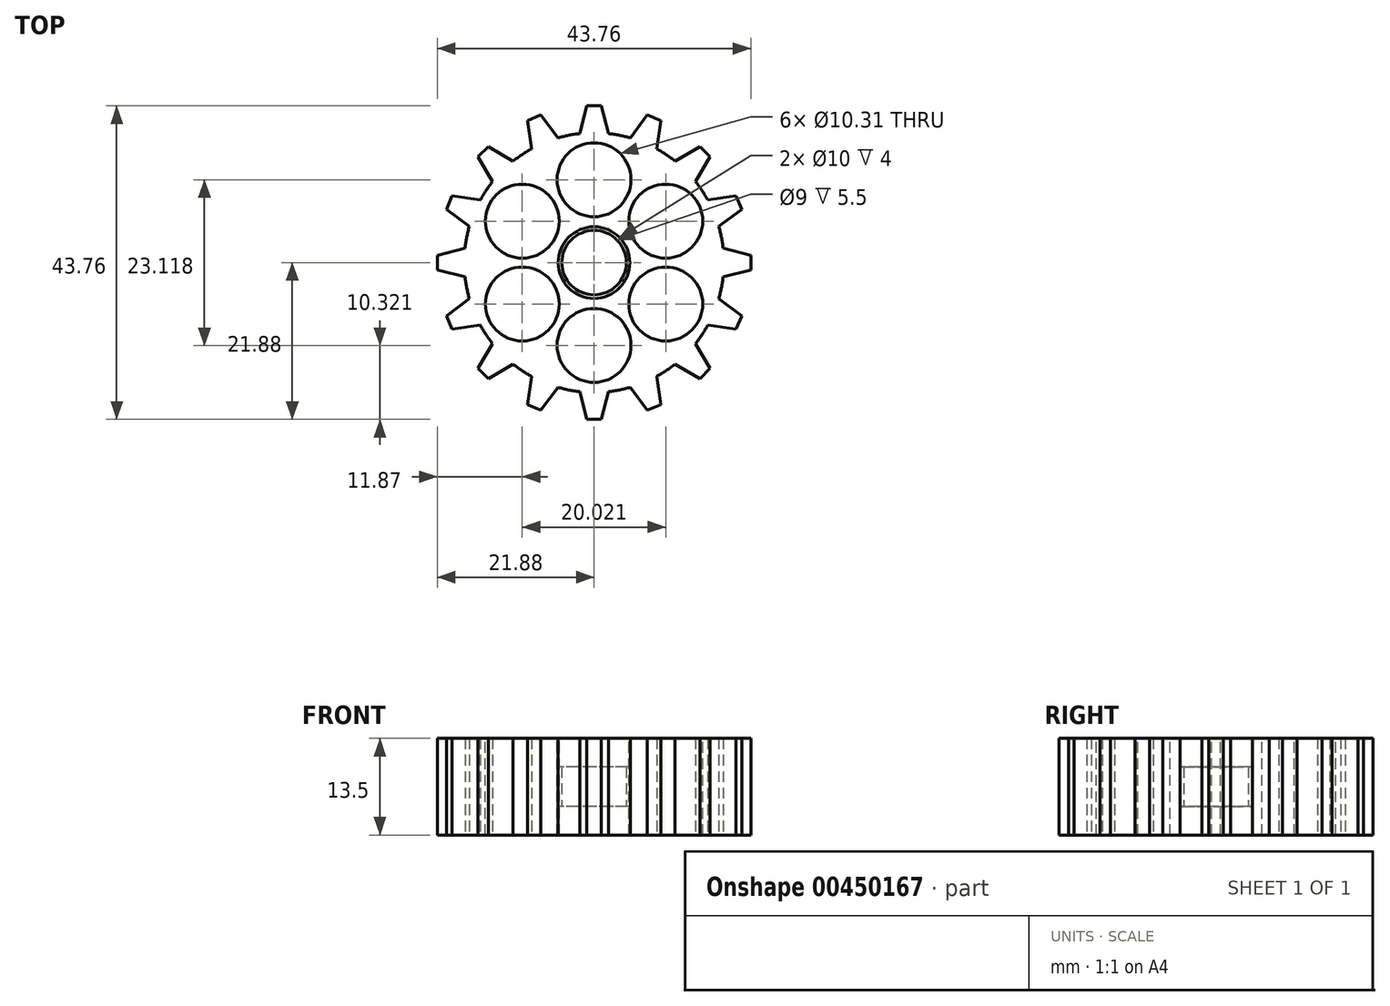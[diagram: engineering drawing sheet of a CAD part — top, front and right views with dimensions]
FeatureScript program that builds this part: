
annotation { "Feature Type Name" : "Feature", "Feature Type Description" : "" }
export const myFeature = defineFeature(function(context is Context, id is Id, definition is map)
    precondition{}
    {
        {
            var Q0;
            Q0=qCreatedBy(makeId("Top.planeOp"),FACE);
            var sketch = newSketch(context, id + "F0", { "sketchPlane" : qUnion([Q0])});
            skLineSegment(sketch, "E0", {"start": v(-18, -2) * mm, "end": v(-21.88, -1) * mm});
            skLineSegment(sketch, "E1", {"start": v(-21.88, -1) * mm, "end": v(-21.88, 1) * mm});
            skLineSegment(sketch, "E2", {"start": v(-21.88, 1) * mm, "end": v(-18, 2) * mm});
            skCircle(sketch, "E3", {"center": v(0, 0) * mm, "radius": 20 * mm, "construction": true});
            skPoint(sketch, "E4", {"position": v(-19.94, 1.5) * mm});
            skPoint(sketch, "E5", {"position": v(-19.94, -1.5) * mm});
            skArc(sketch, "E6", {"start": v(-17.4, 5.04) * mm, "mid": v(-17.77, 3.53) * mm, "end": v(-18, 2) * mm});
            skPoint(sketch, "E7", {"position": v(-21.88, 0) * mm});
            skLineSegment(sketch, "E8.1.0", {"start": v(-15.87, -8.74) * mm, "end": v(-19.83, -9.3) * mm});
            skLineSegment(sketch, "E8.1.1", {"start": v(-20.6, -7.45) * mm, "end": v(-17.4, -5.04) * mm});
            skArc(sketch, "E8.1.2", {"start": v(-18, -2) * mm, "mid": v(-17.77, -3.53) * mm, "end": v(-17.4, -5.04) * mm});
            skPoint(sketch, "E8.1.3", {"position": v(-19, -6.25) * mm});
            skPoint(sketch, "E8.1.4", {"position": v(-17.85, -9.02) * mm});
            skPoint(sketch, "E8.1.5", {"position": v(-20.21, -8.37) * mm});
            skLineSegment(sketch, "E8.1.6", {"start": v(-19.83, -9.3) * mm, "end": v(-20.6, -7.45) * mm});
            skLineSegment(sketch, "E8.2.0", {"start": v(-11.32, -14.15) * mm, "end": v(-14.76, -16.18) * mm});
            skLineSegment(sketch, "E8.2.1", {"start": v(-16.18, -14.76) * mm, "end": v(-14.15, -11.32) * mm});
            skArc(sketch, "E8.2.2", {"start": v(-15.87, -8.74) * mm, "mid": v(-15.06, -10.07) * mm, "end": v(-14.15, -11.32) * mm});
            skPoint(sketch, "E8.2.3", {"position": v(-15.16, -13.04) * mm});
            skPoint(sketch, "E8.2.4", {"position": v(-13.04, -15.16) * mm});
            skPoint(sketch, "E8.2.5", {"position": v(-15.47, -15.47) * mm});
            skLineSegment(sketch, "E8.2.6", {"start": v(-14.76, -16.18) * mm, "end": v(-16.18, -14.76) * mm});
            skLineSegment(sketch, "E8.3.0", {"start": v(-5.04, -17.4) * mm, "end": v(-7.45, -20.6) * mm});
            skLineSegment(sketch, "E8.3.1", {"start": v(-9.3, -19.83) * mm, "end": v(-8.74, -15.87) * mm});
            skArc(sketch, "E8.3.2", {"start": v(-11.32, -14.15) * mm, "mid": v(-10.07, -15.06) * mm, "end": v(-8.74, -15.87) * mm});
            skPoint(sketch, "E8.3.3", {"position": v(-9.02, -17.85) * mm});
            skPoint(sketch, "E8.3.4", {"position": v(-6.25, -19) * mm});
            skPoint(sketch, "E8.3.5", {"position": v(-8.37, -20.21) * mm});
            skLineSegment(sketch, "E8.3.6", {"start": v(-7.45, -20.6) * mm, "end": v(-9.3, -19.83) * mm});
            skLineSegment(sketch, "E8.4.0", {"start": v(2, -18) * mm, "end": v(1, -21.88) * mm});
            skLineSegment(sketch, "E8.4.1", {"start": v(-1, -21.88) * mm, "end": v(-2, -18) * mm});
            skArc(sketch, "E8.4.2", {"start": v(-5.04, -17.4) * mm, "mid": v(-3.53, -17.77) * mm, "end": v(-2, -18) * mm});
            skPoint(sketch, "E8.4.3", {"position": v(-1.5, -19.94) * mm});
            skPoint(sketch, "E8.4.4", {"position": v(1.5, -19.94) * mm});
            skPoint(sketch, "E8.4.5", {"position": v(0, -21.88) * mm});
            skLineSegment(sketch, "E8.4.6", {"start": v(1, -21.88) * mm, "end": v(-1, -21.88) * mm});
            skLineSegment(sketch, "E8.5.0", {"start": v(8.74, -15.87) * mm, "end": v(9.3, -19.83) * mm});
            skLineSegment(sketch, "E8.5.1", {"start": v(7.45, -20.6) * mm, "end": v(5.04, -17.4) * mm});
            skArc(sketch, "E8.5.2", {"start": v(2, -18) * mm, "mid": v(3.53, -17.77) * mm, "end": v(5.04, -17.4) * mm});
            skPoint(sketch, "E8.5.3", {"position": v(6.25, -19) * mm});
            skPoint(sketch, "E8.5.4", {"position": v(9.02, -17.85) * mm});
            skPoint(sketch, "E8.5.5", {"position": v(8.37, -20.21) * mm});
            skLineSegment(sketch, "E8.5.6", {"start": v(9.3, -19.83) * mm, "end": v(7.45, -20.6) * mm});
            skLineSegment(sketch, "E8.6.0", {"start": v(14.15, -11.32) * mm, "end": v(16.18, -14.76) * mm});
            skLineSegment(sketch, "E8.6.1", {"start": v(14.76, -16.18) * mm, "end": v(11.32, -14.15) * mm});
            skArc(sketch, "E8.6.2", {"start": v(8.74, -15.87) * mm, "mid": v(10.07, -15.06) * mm, "end": v(11.32, -14.15) * mm});
            skPoint(sketch, "E8.6.3", {"position": v(13.04, -15.16) * mm});
            skPoint(sketch, "E8.6.4", {"position": v(15.16, -13.04) * mm});
            skPoint(sketch, "E8.6.5", {"position": v(15.47, -15.47) * mm});
            skLineSegment(sketch, "E8.6.6", {"start": v(16.18, -14.76) * mm, "end": v(14.76, -16.18) * mm});
            skLineSegment(sketch, "E8.7.0", {"start": v(17.4, -5.04) * mm, "end": v(20.6, -7.45) * mm});
            skLineSegment(sketch, "E8.7.1", {"start": v(19.83, -9.3) * mm, "end": v(15.87, -8.74) * mm});
            skArc(sketch, "E8.7.2", {"start": v(14.15, -11.32) * mm, "mid": v(15.06, -10.07) * mm, "end": v(15.87, -8.74) * mm});
            skPoint(sketch, "E8.7.3", {"position": v(17.85, -9.02) * mm});
            skPoint(sketch, "E8.7.4", {"position": v(19, -6.25) * mm});
            skPoint(sketch, "E8.7.5", {"position": v(20.21, -8.37) * mm});
            skLineSegment(sketch, "E8.7.6", {"start": v(20.6, -7.45) * mm, "end": v(19.83, -9.3) * mm});
            skLineSegment(sketch, "E8.8.0", {"start": v(18, 2) * mm, "end": v(21.88, 1) * mm});
            skLineSegment(sketch, "E8.8.1", {"start": v(21.88, -1) * mm, "end": v(18, -2) * mm});
            skArc(sketch, "E8.8.2", {"start": v(17.4, -5.04) * mm, "mid": v(17.77, -3.53) * mm, "end": v(18, -2) * mm});
            skPoint(sketch, "E8.8.3", {"position": v(19.94, -1.5) * mm});
            skPoint(sketch, "E8.8.4", {"position": v(19.94, 1.5) * mm});
            skPoint(sketch, "E8.8.5", {"position": v(21.88, 0) * mm});
            skLineSegment(sketch, "E8.8.6", {"start": v(21.88, 1) * mm, "end": v(21.88, -1) * mm});
            skLineSegment(sketch, "E8.9.0", {"start": v(15.87, 8.74) * mm, "end": v(19.83, 9.3) * mm});
            skLineSegment(sketch, "E8.9.1", {"start": v(20.6, 7.45) * mm, "end": v(17.4, 5.04) * mm});
            skArc(sketch, "E8.9.2", {"start": v(18, 2) * mm, "mid": v(17.77, 3.53) * mm, "end": v(17.4, 5.04) * mm});
            skPoint(sketch, "E8.9.3", {"position": v(19, 6.25) * mm});
            skPoint(sketch, "E8.9.4", {"position": v(17.85, 9.02) * mm});
            skPoint(sketch, "E8.9.5", {"position": v(20.21, 8.37) * mm});
            skLineSegment(sketch, "E8.9.6", {"start": v(19.83, 9.3) * mm, "end": v(20.6, 7.45) * mm});
            skLineSegment(sketch, "E8.10.0", {"start": v(11.32, 14.15) * mm, "end": v(14.76, 16.18) * mm});
            skLineSegment(sketch, "E8.10.1", {"start": v(16.18, 14.76) * mm, "end": v(14.15, 11.32) * mm});
            skArc(sketch, "E8.10.2", {"start": v(15.87, 8.74) * mm, "mid": v(15.06, 10.07) * mm, "end": v(14.15, 11.32) * mm});
            skPoint(sketch, "E8.10.3", {"position": v(15.16, 13.04) * mm});
            skPoint(sketch, "E8.10.4", {"position": v(13.04, 15.16) * mm});
            skPoint(sketch, "E8.10.5", {"position": v(15.47, 15.47) * mm});
            skLineSegment(sketch, "E8.10.6", {"start": v(14.76, 16.18) * mm, "end": v(16.18, 14.76) * mm});
            skLineSegment(sketch, "E8.11.0", {"start": v(5.04, 17.4) * mm, "end": v(7.45, 20.6) * mm});
            skLineSegment(sketch, "E8.11.1", {"start": v(9.3, 19.83) * mm, "end": v(8.74, 15.87) * mm});
            skArc(sketch, "E8.11.2", {"start": v(11.32, 14.15) * mm, "mid": v(10.07, 15.06) * mm, "end": v(8.74, 15.87) * mm});
            skPoint(sketch, "E8.11.3", {"position": v(9.02, 17.85) * mm});
            skPoint(sketch, "E8.11.4", {"position": v(6.25, 19) * mm});
            skPoint(sketch, "E8.11.5", {"position": v(8.37, 20.21) * mm});
            skLineSegment(sketch, "E8.11.6", {"start": v(7.45, 20.6) * mm, "end": v(9.3, 19.83) * mm});
            skCircle(sketch, "E9", {"center": v(0, 0) * mm, "radius": 5 * mm});
            skCircle(sketch, "E10", {"center": v(0, 0) * mm, "radius": 4.5 * mm});
            skLineSegment(sketch, "E11.2.12.0", {"start": v(-2, 18) * mm, "end": v(-1, 21.88) * mm});
            skLineSegment(sketch, "E11.3.12.0", {"start": v(1, 21.88) * mm, "end": v(2, 18) * mm});
            skArc(sketch, "E11.6.12.0", {"start": v(5.04, 17.4) * mm, "mid": v(3.53, 17.77) * mm, "end": v(2, 18) * mm});
            skPoint(sketch, "E11.10.12.0", {"position": v(1.5, 19.94) * mm});
            skPoint(sketch, "E11.11.12.0", {"position": v(-1.5, 19.94) * mm});
            skPoint(sketch, "E11.12.12.0", {"position": v(0, 21.88) * mm});
            skLineSegment(sketch, "E11.13.12.0", {"start": v(-1, 21.88) * mm, "end": v(1, 21.88) * mm});
            skLineSegment(sketch, "E11.2.13.0", {"start": v(-8.74, 15.87) * mm, "end": v(-9.3, 19.83) * mm});
            skLineSegment(sketch, "E11.3.13.0", {"start": v(-7.45, 20.6) * mm, "end": v(-5.04, 17.4) * mm});
            skArc(sketch, "E11.6.13.0", {"start": v(-2, 18) * mm, "mid": v(-3.53, 17.77) * mm, "end": v(-5.04, 17.4) * mm});
            skPoint(sketch, "E11.10.13.0", {"position": v(-6.25, 19) * mm});
            skPoint(sketch, "E11.11.13.0", {"position": v(-9.02, 17.85) * mm});
            skPoint(sketch, "E11.12.13.0", {"position": v(-8.37, 20.21) * mm});
            skLineSegment(sketch, "E11.13.13.0", {"start": v(-9.3, 19.83) * mm, "end": v(-7.45, 20.6) * mm});
            skLineSegment(sketch, "E11.2.14.0", {"start": v(-14.15, 11.32) * mm, "end": v(-16.18, 14.76) * mm});
            skLineSegment(sketch, "E11.3.14.0", {"start": v(-14.76, 16.18) * mm, "end": v(-11.32, 14.15) * mm});
            skArc(sketch, "E11.6.14.0", {"start": v(-8.74, 15.87) * mm, "mid": v(-10.07, 15.06) * mm, "end": v(-11.32, 14.15) * mm});
            skPoint(sketch, "E11.10.14.0", {"position": v(-13.04, 15.16) * mm});
            skPoint(sketch, "E11.11.14.0", {"position": v(-15.16, 13.04) * mm});
            skPoint(sketch, "E11.12.14.0", {"position": v(-15.47, 15.47) * mm});
            skLineSegment(sketch, "E11.13.14.0", {"start": v(-16.18, 14.76) * mm, "end": v(-14.76, 16.18) * mm});
            skLineSegment(sketch, "E11.2.15.0", {"start": v(-17.4, 5.04) * mm, "end": v(-20.6, 7.45) * mm});
            skLineSegment(sketch, "E11.3.15.0", {"start": v(-19.83, 9.3) * mm, "end": v(-15.87, 8.74) * mm});
            skArc(sketch, "E11.6.15.0", {"start": v(-14.15, 11.32) * mm, "mid": v(-15.06, 10.07) * mm, "end": v(-15.87, 8.74) * mm});
            skPoint(sketch, "E11.10.15.0", {"position": v(-17.85, 9.02) * mm});
            skPoint(sketch, "E11.11.15.0", {"position": v(-19, 6.25) * mm});
            skPoint(sketch, "E11.12.15.0", {"position": v(-20.21, 8.37) * mm});
            skLineSegment(sketch, "E11.13.15.0", {"start": v(-20.6, 7.45) * mm, "end": v(-19.83, 9.3) * mm});
            skSolve(sketch);
        }
        {
            var Q0;
            Q0 = qSketchRegion(id + "F0", true);
            extrude(context, id + "F1", {"entities" : qUnion([Q0]), "endBound" : BoundingType.SYMMETRIC, "depth" : 13.5 * mm});
        }
        {
            var Q0;
            Q0=makeQuery(id+"F0.imprint","IMPRINT",FACE,{"disambiguationData":[TD([[makeQuery(id+"F0.imprint","IMPRINT",EDGE,{"derivedFrom":sQuery(id+"F0.wireOp",EDGE,"E9")}),1.0]])]});
            extrude(context, id + "F2", {"entities" : qUnion([Q0]), "operationType" : NewBodyOperationType.ADD, "endBound" : BoundingType.SYMMETRIC, "depth" : 5.5 * mm});
        }
        {
            var Q0;
            Q0=makeQuery(id+"F1.opExtrude","CAP_FACE",FACE,{"disambiguationData":[OSD([sQuery(id+"F0.wireOp",EDGE,"E0"),sQuery(id+"F0.wireOp",EDGE,"E1"),sQuery(id+"F0.wireOp",EDGE,"E2"),sQuery(id+"F0.wireOp",EDGE,"E6"),sQuery(id+"F0.wireOp",EDGE,"E8.1.0"),sQuery(id+"F0.wireOp",EDGE,"E8.1.1"),sQuery(id+"F0.wireOp",EDGE,"E8.1.2"),sQuery(id+"F0.wireOp",EDGE,"E8.1.6"),sQuery(id+"F0.wireOp",EDGE,"E8.2.0"),sQuery(id+"F0.wireOp",EDGE,"E8.2.1"),sQuery(id+"F0.wireOp",EDGE,"E8.2.2"),sQuery(id+"F0.wireOp",EDGE,"E8.2.6"),sQuery(id+"F0.wireOp",EDGE,"E8.3.0"),sQuery(id+"F0.wireOp",EDGE,"E8.3.1"),sQuery(id+"F0.wireOp",EDGE,"E8.3.2"),sQuery(id+"F0.wireOp",EDGE,"E8.3.6"),sQuery(id+"F0.wireOp",EDGE,"E8.4.0"),sQuery(id+"F0.wireOp",EDGE,"E8.4.1"),sQuery(id+"F0.wireOp",EDGE,"E8.4.2"),sQuery(id+"F0.wireOp",EDGE,"E8.4.6"),sQuery(id+"F0.wireOp",EDGE,"E8.5.0"),sQuery(id+"F0.wireOp",EDGE,"E8.5.1"),sQuery(id+"F0.wireOp",EDGE,"E8.5.2"),sQuery(id+"F0.wireOp",EDGE,"E8.5.6"),sQuery(id+"F0.wireOp",EDGE,"E8.6.0"),sQuery(id+"F0.wireOp",EDGE,"E8.6.1"),sQuery(id+"F0.wireOp",EDGE,"E8.6.2"),sQuery(id+"F0.wireOp",EDGE,"E8.6.6"),sQuery(id+"F0.wireOp",EDGE,"E8.7.0"),sQuery(id+"F0.wireOp",EDGE,"E8.7.1"),sQuery(id+"F0.wireOp",EDGE,"E8.7.2"),sQuery(id+"F0.wireOp",EDGE,"E8.7.6"),sQuery(id+"F0.wireOp",EDGE,"E8.8.0"),sQuery(id+"F0.wireOp",EDGE,"E8.8.1"),sQuery(id+"F0.wireOp",EDGE,"E8.8.2"),sQuery(id+"F0.wireOp",EDGE,"E8.8.6"),sQuery(id+"F0.wireOp",EDGE,"E8.9.0"),sQuery(id+"F0.wireOp",EDGE,"E8.9.1"),sQuery(id+"F0.wireOp",EDGE,"E8.9.2"),sQuery(id+"F0.wireOp",EDGE,"E8.9.6"),sQuery(id+"F0.wireOp",EDGE,"E8.10.0"),sQuery(id+"F0.wireOp",EDGE,"E8.10.1"),sQuery(id+"F0.wireOp",EDGE,"E8.10.2"),sQuery(id+"F0.wireOp",EDGE,"E8.10.6"),sQuery(id+"F0.wireOp",EDGE,"E8.11.0"),sQuery(id+"F0.wireOp",EDGE,"E8.11.1"),sQuery(id+"F0.wireOp",EDGE,"E8.11.2"),sQuery(id+"F0.wireOp",EDGE,"E8.11.6"),sQuery(id+"F0.wireOp",EDGE,"E9")])],"isStart":false});
            var sketch = newSketch(context, id + "F3", { "sketchPlane" : qUnion([Q0])});
            skCircle(sketch, "E12", {"center": v(0, 11.56) * mm, "radius": 5.15 * mm});
            skLineSegment(sketch, "E13", {"start": v(0, 5) * mm, "end": v(0, 18.12) * mm, "construction": true});
            skArc(sketch, "E14", {"start": v(17.4, 5.04) * mm, "mid": v(16.74, 6.93) * mm, "end": v(15.87, 8.74) * mm, "construction": true});
            skLineSegment(sketch, "E15.1.0", {"start": v(-4.33, 2.5) * mm, "end": v(-15.7, 9.06) * mm, "construction": true});
            skCircle(sketch, "E15.1.1", {"center": v(-10.01, 5.78) * mm, "radius": 5.15 * mm});
            skArc(sketch, "E15.1.2", {"start": v(4.33, 17.6) * mm, "mid": v(2.36, 17.96) * mm, "end": v(0.37, 18.11) * mm, "construction": true});
            skLineSegment(sketch, "E15.2.0", {"start": v(-4.33, -2.5) * mm, "end": v(-15.7, -9.06) * mm, "construction": true});
            skCircle(sketch, "E15.2.1", {"center": v(-10.01, -5.78) * mm, "radius": 5.15 * mm});
            skArc(sketch, "E15.2.2", {"start": v(-13.07, 12.55) * mm, "mid": v(-14.37, 11.03) * mm, "end": v(-15.5, 9.38) * mm, "construction": true});
            skLineSegment(sketch, "E16.1.3.0", {"start": v(0, -5) * mm, "end": v(0, -18.12) * mm, "construction": true});
            skCircle(sketch, "E16.3.3.0", {"center": v(0, -11.56) * mm, "radius": 5.15 * mm});
            skArc(sketch, "E16.5.3.0", {"start": v(-17.4, -5.04) * mm, "mid": v(-16.74, -6.93) * mm, "end": v(-15.87, -8.74) * mm, "construction": true});
            skLineSegment(sketch, "E16.1.4.0", {"start": v(4.33, -2.5) * mm, "end": v(15.7, -9.06) * mm, "construction": true});
            skCircle(sketch, "E16.3.4.0", {"center": v(10.01, -5.78) * mm, "radius": 5.15 * mm});
            skArc(sketch, "E16.5.4.0", {"start": v(-4.33, -17.6) * mm, "mid": v(-2.36, -17.96) * mm, "end": v(-0.37, -18.11) * mm, "construction": true});
            skLineSegment(sketch, "E16.1.5.0", {"start": v(4.33, 2.5) * mm, "end": v(15.7, 9.06) * mm, "construction": true});
            skCircle(sketch, "E16.3.5.0", {"center": v(10.01, 5.78) * mm, "radius": 5.15 * mm});
            skArc(sketch, "E16.5.5.0", {"start": v(13.07, -12.55) * mm, "mid": v(14.37, -11.03) * mm, "end": v(15.5, -9.38) * mm, "construction": true});
            skSolve(sketch);
        }
        {
            var Q0;
            Q0 = qSketchRegion(id + "F3", true);
            extrude(context, id + "F4", {"entities" : qUnion([Q0]), "operationType" : NewBodyOperationType.REMOVE, "endBound" : BoundingType.THROUGH_ALL, "oppositeDirection" : true, "depth" : 25 * mm});
        }
    });
